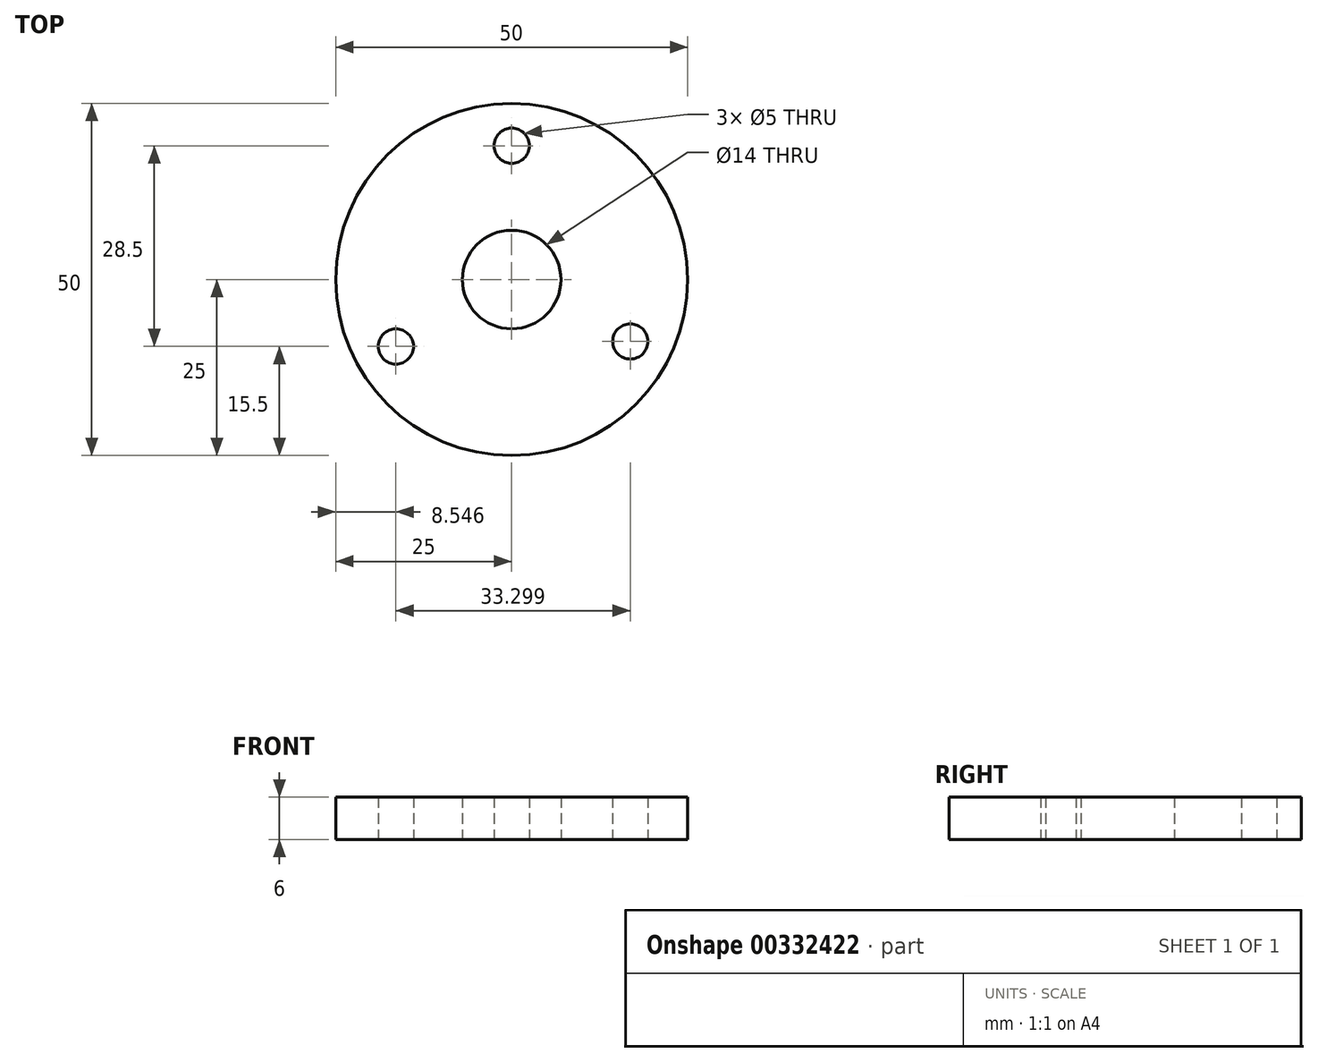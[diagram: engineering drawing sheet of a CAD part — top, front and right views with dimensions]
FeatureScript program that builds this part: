
annotation { "Feature Type Name" : "Feature", "Feature Type Description" : "" }
export const myFeature = defineFeature(function(context is Context, id is Id, definition is map)
    precondition{}
    {
        {
            var Q0;
            Q0=qCreatedBy(makeId("Top.planeOp"),FACE);
            var sketch = newSketch(context, id + "F0", { "sketchPlane" : qUnion([Q0])});
            skCircle(sketch, "E0", {"center": v(0, 0) * mm, "radius": 25 * mm});
            skCircle(sketch, "E1", {"center": v(0, 0) * mm, "radius": 7 * mm});
            skCircle(sketch, "E2", {"center": v(0, 19) * mm, "radius": 2.5 * mm});
            skCircle(sketch, "E3", {"center": v(-16.45, -9.5) * mm, "radius": 2.5 * mm});
            skCircle(sketch, "E4", {"center": v(16.84, -8.79) * mm, "radius": 2.5 * mm});
            skLineSegment(sketch, "E5", {"start": v(0, 0) * mm, "end": v(16.84, -8.79) * mm});
            skSolve(sketch);
        }
        {
            var Q0;
            Q0 = qSketchRegion(id + "F0", true);
            extrude(context, id + "F1", {"entities" : qUnion([Q0]), "depth" : 6 * mm});
        }
    });
